# Revit family: Towel_Dispenser-Bradley_Corp-2483
name_source: partatom
category: Specialty Equipment
revit_build: Autodesk Revit MEP 2012 (Build: 20110309_2315(x64)
units: mm (PartAtom-declared; Revit-internal decimal feet)

## types (1)
- Towel_Dispenser-Bradley_Corp-2483
    ADA Compliant = Yes
    Assembly Code = C1030200
    Buy American Act = Yes
    Cabinet Material = Metal - Bradley Corp - Stainless Steel - Satin
    Default Elevation = 48"
    Depth = 10 3/8"
    Depth Cabinet = 9"
    Description = Towel Dispenser
    Height = 15"
    Manufacturer = Bradley Corporation
    MasterFormat Number = 10 28 13. 13
    MasterFormat Title = Toilet Accessories
    Model = 2483-000000
    OmniClass Table 21 Number = 21-03 10 90 40
    OmniClass Table 21 Title = Toilet, Bath, and Laundry Accessories
    OmniClass Table 23 Number = 23-31 25 19 11
    OmniClass Table 23 Title = Paper Towel Dispenser/Disposal Unit
    Product Tech Data URL - English = http://bradleycorp.com
    Specifications URL = http://www.bradleycorp.com
    Tower Lip Material = Plastic - Bradley Corp - White
    URL = http://www.bradleycorp.com
    Version = 2.0
    Warranty Information = Complete unit, excepting mirrors warranted for one year.
 Stainless steel mirror frames for fifteen years.
 Plate glass mirrors for fifteen years.
 This warranty does not cover installation or any other labor charges and does not apply to any units,
 which have been damaged by accident, abuse, improper installation, improper maintenance, or altered in any way.
    Width = 12 1/4"

## geometry (parser evidence)
native form markers: Blend x4, Sweep x1
no freeform markers — native parametric forms only
